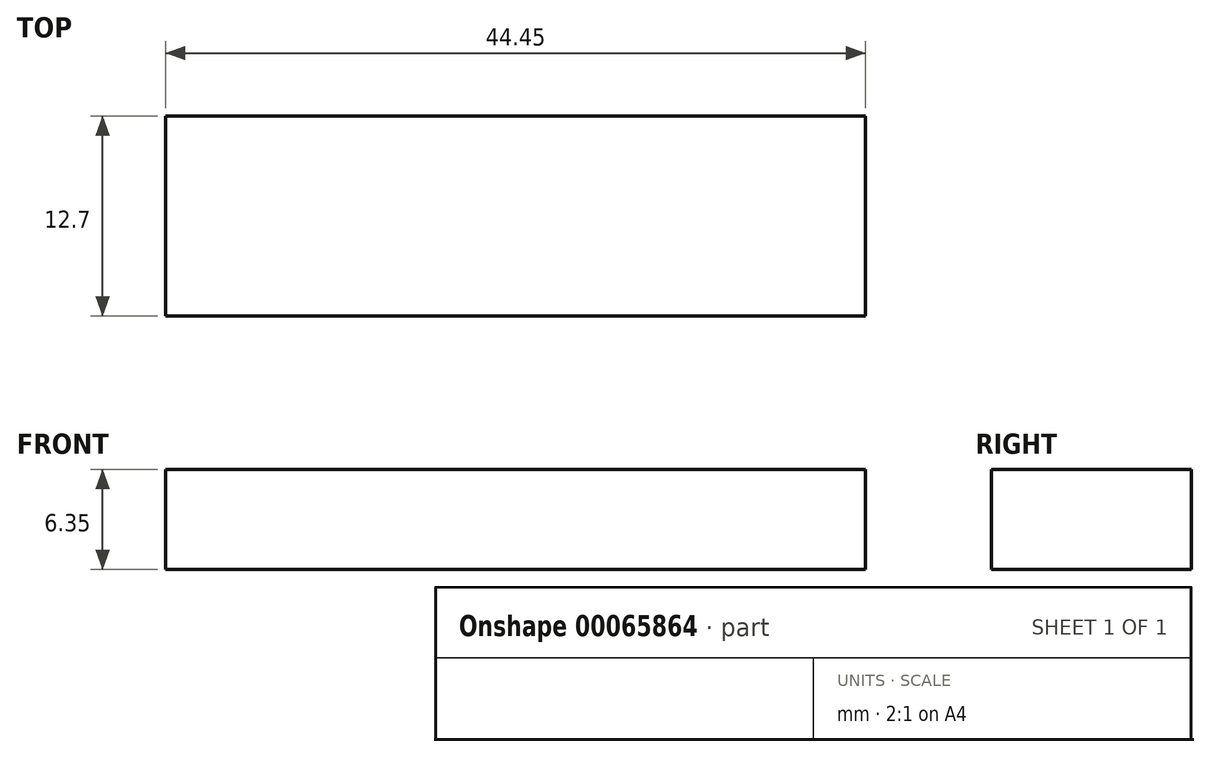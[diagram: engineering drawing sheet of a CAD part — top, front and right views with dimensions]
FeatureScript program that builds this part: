
annotation { "Feature Type Name" : "Feature", "Feature Type Description" : "" }
export const myFeature = defineFeature(function(context is Context, id is Id, definition is map)
    precondition{}
    {
        {
            var Q0;
            Q0=qCreatedBy(makeId("Top.planeOp"),FACE);
            var sketch = newSketch(context, id + "F0", { "sketchPlane" : qUnion([Q0])});
            skLineSegment(sketch, "E0.bottom", {"start": v(0, 0) * mm, "end": v(44.45, 0) * mm});
            skLineSegment(sketch, "E0.top", {"start": v(0, -12.7) * mm, "end": v(44.45, -12.7) * mm});
            skLineSegment(sketch, "E0.left", {"start": v(0, 0) * mm, "end": v(0, -12.7) * mm});
            skLineSegment(sketch, "E0.right", {"start": v(44.45, 0) * mm, "end": v(44.45, -12.7) * mm});
            skSolve(sketch);
        }
        {
            var Q0;
            Q0=makeQuery(id+"F0.imprint","IMPRINT",FACE,{"disambiguationData":[TD([[makeQuery(id+"F0.imprint","IMPRINT",EDGE,{"derivedFrom":sQuery(id+"F0.wireOp",EDGE,"E0.bottom")}),-1.0]])]});
            extrude(context, id + "F1", {"entities" : qUnion([Q0]), "depth" : 6.35 * mm});
        }
    });
